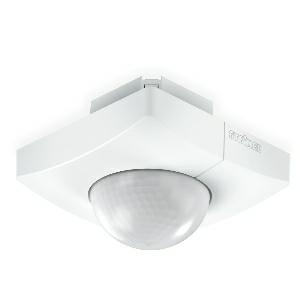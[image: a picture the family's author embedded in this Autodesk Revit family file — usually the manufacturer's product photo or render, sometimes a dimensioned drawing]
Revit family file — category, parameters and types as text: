
# Revit family: is_345_057282
name_source: partatom
category: Elektroinstallationen
revit_build: Autodesk Revit 2016 (Build: 20190508_0715(x64)
units: mm (PartAtom-declared; Revit-internal decimal feet)

## family parameters
Basisbauteil = Fläche
Beim Laden mit Abzugskörper schneiden = Nein
Bemaßung runder Anschluss = Durchmesser verwenden
Beschriftungsausrichtung beibehalten = Nein
Gemeinsam genutzt = Nein
Raumberechnungspunkt = Nein
Teiletyp = Normal

## types (1)
- IS 345
    Apparent Load = 0 VA
    Beschreibung = Type: Motion detectors; Dimensions (L x W x H): 78 x 94 x 94 mm; Mains power supply: 12 – 22,5 V / 50 – 60 Hz; Sensor Technology: passive infrared; Application, place: Indoors; Application, room: corridor / aisle, multi-storey / underground car park, Indoors; Installation site: ceiling; Installation: Concealed wiring; Switching zones: 280 switching zones; Electronic scalability: No; Mechanical scalability: No; Mounting height: 2,5 – 5 m; Optimum mounting height: 2,8 m; Detection angle: 360 °; Angle of aperture: 45 °; Sneak-by guard: Yes; Capability of masking out individual segments: Yes; Reach, radial: 12 x 6 m (72 m²); Reach, tangential: 23 x 6 m (138 m²); Twilight setting TEACH: Yes; Twilight setting: 2 – 1000 lx; Time setting: 5 sec – 15 min; Control output, Dali: Addressable/slave; Constant-lighting control: No; Basic light level function: No; Basic light level function time: 1-30 min, all night; With bus coupling: Yes; Settings via: Bus; With remote control: No; Interconnection: Yes; IP-rating: IP20; Material: Plastic; Ambient temperature: -20 – 50 °C; Colour: white; Colour, RAL: 9003; Manufacturer's Warranty: 5 years; Version: DALI-2 IPD - concealed, sq.; PU1, EAN: 4007841057282
    Height = 0 mm  [stored 0 ft]
    Hersteller = Steinel
    Length = 78 mm  [stored 0.255906 ft]
    Maximum range = 11.589 m
    ModVariant = Nein
    Modell = 057282
    Mounting Place = Ceiling
    Mounting Type = Recessed
    Number of Poles = 1
    OnlyDefault = Ja
    Power Factor = 1
    Product Name = IS 345
    Product group = Presence detector
    ProductGroupID = 4
    Protection Class = Protection class
    Protection Degree = IP 20
    RlxData = <blob elided: 137213 chars, md5=9e5332fa>
    Sensor characteristics = Stretched
    Sensor type = Passive (infrared)
    SensorDataFile = <blob elided: 5885 chars, md5=98bccc25>
    Type of entry = Motion
    Typenbild = produkt1_057282.jpg
    Typenkommentare = Product without accessories
    URL = http://relux.com
    VarID = ---
    Voltage = 0 V
    Vorgabe-Ansicht = 1800 mm
    Weight = 0.00 kg
    Width = 94 mm  [stored 0.308399 ft]

note: [stored X ft] marks values corroborated as IEEE doubles in the binary element streams (Revit-internal decimal feet)

## geometry (parser evidence)
native form markers: Sweep x17
no freeform markers — native parametric forms only
